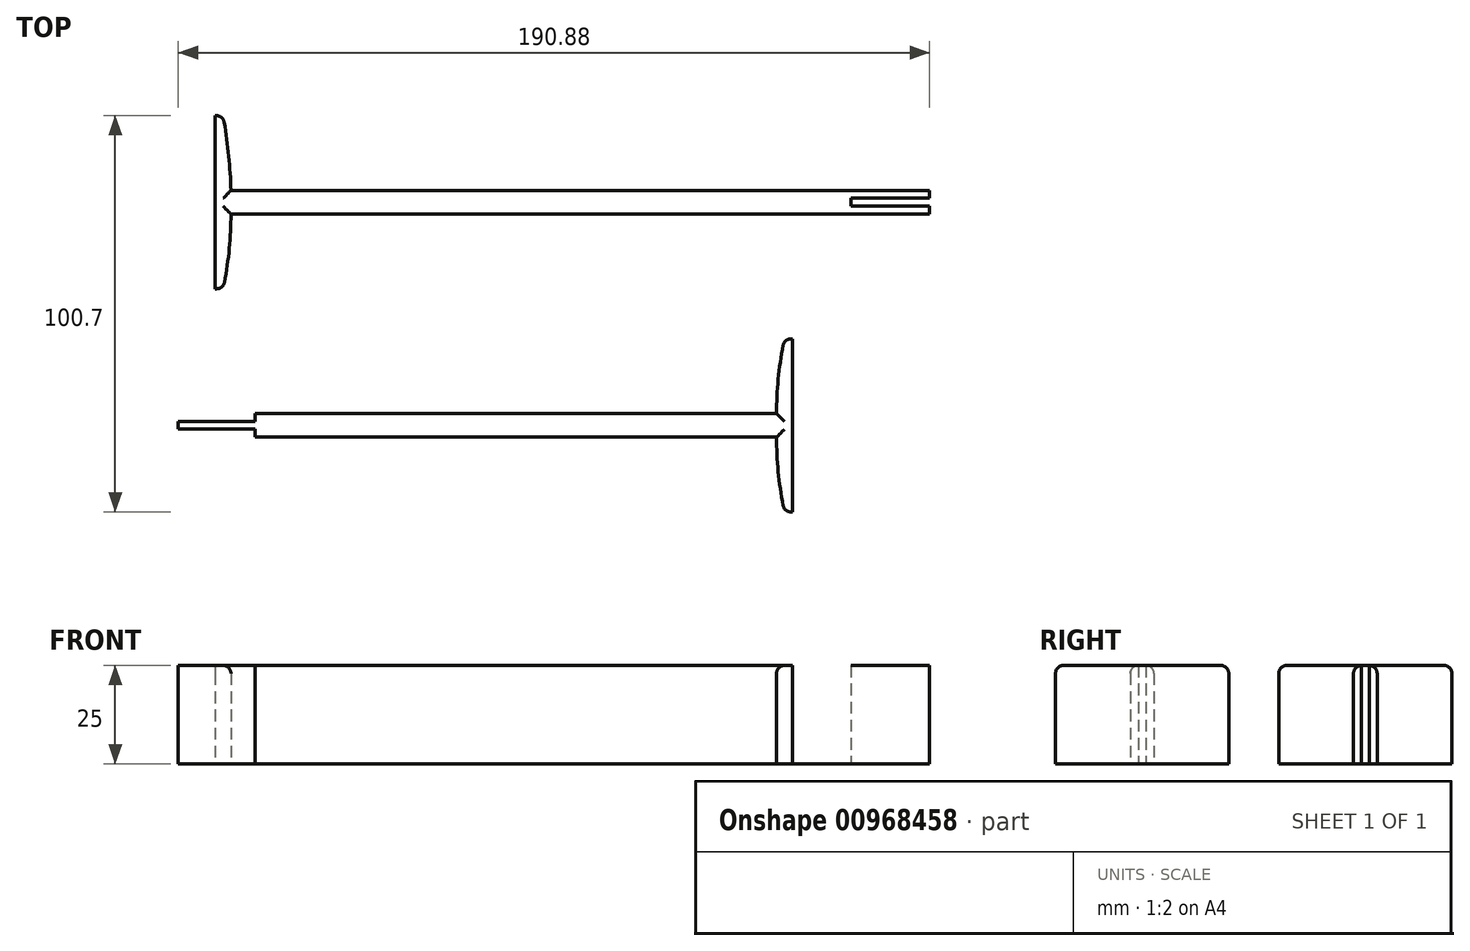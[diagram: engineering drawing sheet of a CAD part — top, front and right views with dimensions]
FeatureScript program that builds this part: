
annotation { "Feature Type Name" : "Feature", "Feature Type Description" : "" }
export const myFeature = defineFeature(function(context is Context, id is Id, definition is map)
    precondition{}
    {
        {
            var Q0;
            Q0=qCreatedBy(makeId("Top.planeOp"),FACE);
            var sketch = newSketch(context, id + "F0", { "sketchPlane" : qUnion([Q0])});
            skLineSegment(sketch, "E0.bottom", {"start": v(-53.26, 18.7) * mm, "end": v(104.24, 18.7) * mm});
            skLineSegment(sketch, "E0.top", {"start": v(-53.26, 12.7) * mm, "end": v(104.24, 12.7) * mm});
            skLineSegment(sketch, "E0.left", {"start": v(-53.26, 18.7) * mm, "end": v(-53.26, 12.7) * mm});
            skLineSegment(sketch, "E0.right", {"start": v(104.24, 18.7) * mm, "end": v(104.24, 12.7) * mm});
            skLineSegment(sketch, "E1.bottom", {"start": v(104.24, 18.7) * mm, "end": v(124.24, 18.7) * mm});
            skLineSegment(sketch, "E1.top", {"start": v(104.24, 16.7) * mm, "end": v(124.24, 16.7) * mm});
            skLineSegment(sketch, "E1.left", {"start": v(104.24, 18.7) * mm, "end": v(104.24, 16.7) * mm});
            skLineSegment(sketch, "E1.right", {"start": v(124.24, 18.7) * mm, "end": v(124.24, 16.7) * mm});
            skLineSegment(sketch, "E2.bottom", {"start": v(104.24, 12.7) * mm, "end": v(124.24, 12.7) * mm});
            skLineSegment(sketch, "E2.top", {"start": v(104.24, 14.7) * mm, "end": v(124.24, 14.7) * mm});
            skLineSegment(sketch, "E2.left", {"start": v(104.24, 12.7) * mm, "end": v(104.24, 14.7) * mm});
            skLineSegment(sketch, "E2.right", {"start": v(124.24, 12.7) * mm, "end": v(124.24, 14.7) * mm});
            skLineSegment(sketch, "E3", {"start": v(-57.26, 37.7) * mm, "end": v(-55.26, 37.7) * mm});
            skLineSegment(sketch, "E4", {"start": v(-57.26, -6.3) * mm, "end": v(-55.26, -6.3) * mm});
            skLineSegment(sketch, "E5", {"start": v(-57.26, -6.3) * mm, "end": v(-57.26, 37.7) * mm});
            skLineSegment(sketch, "E6", {"start": v(-53.26, 18.69) * mm, "end": v(-53.26, 18.7) * mm});
            skLineSegment(sketch, "E7", {"start": v(-53.26, 18.7) * mm, "end": v(-53.26, 18.69) * mm});
            skArc(sketch, "E8", {"start": v(-55.26, -6.3) * mm, "mid": v(-53.76, 3.14) * mm, "end": v(-53.26, 12.7) * mm});
            skArc(sketch, "E9", {"start": v(-53.26, 18.7) * mm, "mid": v(-53.92, 28.23) * mm, "end": v(-55.26, 37.7) * mm});
            skSolve(sketch);
        }
        {
            var Q0;
            Q0=qCreatedBy(makeId("Top.planeOp"),FACE);
            var sketch = newSketch(context, id + "F1", { "sketchPlane" : qUnion([Q0])});
            skLineSegment(sketch, "E10.MirrorCS", {"start": v(-47.14, -38.01) * mm, "end": v(-47.14, -42.01) * mm});
            skLineSegment(sketch, "E11.MirrorCS", {"start": v(-47.14, -38.01) * mm, "end": v(-47.14, -44.01) * mm});
            skLineSegment(sketch, "E12.MirrorCS", {"start": v(85.36, -38.01) * mm, "end": v(85.36, -44.01) * mm});
            skLineSegment(sketch, "E13.MirrorCS", {"start": v(85.36, -44.01) * mm, "end": v(-47.14, -44.01) * mm});
            skLineSegment(sketch, "E14.MirrorCS", {"start": v(85.36, -38.01) * mm, "end": v(-47.14, -38.01) * mm});
            skLineSegment(sketch, "E15.bottom", {"start": v(-47.14, -40.06) * mm, "end": v(-66.64, -40.06) * mm});
            skLineSegment(sketch, "E15.top", {"start": v(-47.14, -41.96) * mm, "end": v(-66.64, -41.96) * mm});
            skLineSegment(sketch, "E15.left", {"start": v(-47.14, -40.06) * mm, "end": v(-47.14, -41.96) * mm});
            skLineSegment(sketch, "E15.right", {"start": v(-66.64, -40.06) * mm, "end": v(-66.64, -41.96) * mm});
            skLineSegment(sketch, "E16", {"start": v(87.36, -19.01) * mm, "end": v(89.36, -19.01) * mm});
            skLineSegment(sketch, "E17", {"start": v(87.36, -63.01) * mm, "end": v(89.36, -63.01) * mm});
            skLineSegment(sketch, "E18", {"start": v(89.36, -63.01) * mm, "end": v(89.36, -19.01) * mm});
            skArc(sketch, "E19", {"start": v(87.36, -19.01) * mm, "mid": v(85.86, -28.46) * mm, "end": v(85.36, -38.01) * mm});
            skArc(sketch, "E20", {"start": v(85.36, -44.01) * mm, "mid": v(85.86, -53.56) * mm, "end": v(87.36, -63.01) * mm});
            skSolve(sketch);
        }
        {
            var Q0;
            Q0=makeQuery(id+"F1.imprint","IMPRINT",FACE,{"disambiguationData":[TD([[makeQuery(id+"F1.imprint","IMPRINT",EDGE,{"derivedFrom":sQuery(id+"F1.wireOp",EDGE,"E12.MirrorCS")}),1.0]])]});
            var Q1;
            Q1=makeQuery(id+"F1.imprint","IMPRINT",FACE,{"disambiguationData":[TD([[makeQuery(id+"F1.imprint","IMPRINT",EDGE,{"derivedFrom":sQuery(id+"F1.wireOp",EDGE,"E12.MirrorCS")}),-1.0]])]});
            var Q2;
            Q2=makeQuery(id+"F1.imprint","IMPRINT",FACE,{"disambiguationData":[TD([[makeQuery(id+"F1.imprint","IMPRINT",EDGE,{"derivedFrom":sQuery(id+"F1.wireOp",EDGE,"E15.bottom")}),1.0]])]});
            var Q3;
            Q3=makeQuery(id+"F0.imprint","IMPRINT",FACE,{"disambiguationData":[TD([[makeQuery(id+"F0.imprint","IMPRINT",EDGE,{"derivedFrom":sQuery(id+"F0.wireOp",EDGE,"E0.left")}),-1.0]])]});
            var Q4;
            Q4=makeQuery(id+"F0.imprint","IMPRINT",FACE,{"disambiguationData":[TD([[makeQuery(id+"F0.imprint","IMPRINT",EDGE,{"derivedFrom":sQuery(id+"F0.wireOp",EDGE,"E0.bottom")}),-1.0]])]});
            var Q5;
            Q5=makeQuery(id+"F0.imprint","IMPRINT",FACE,{"disambiguationData":[TD([[makeQuery(id+"F0.imprint","IMPRINT",EDGE,{"derivedFrom":sQuery(id+"F0.wireOp",EDGE,"E1.bottom")}),-1.0]])]});
            var Q6;
            Q6=makeQuery(id+"F0.imprint","IMPRINT",FACE,{"disambiguationData":[TD([[makeQuery(id+"F0.imprint","IMPRINT",EDGE,{"derivedFrom":sQuery(id+"F0.wireOp",EDGE,"E2.bottom")}),1.0]])]});
            extrude(context, id + "F2", {"entities" : qUnion([Q0, Q1, Q2, Q3, Q4, Q5, Q6]), "depth" : 25 * mm, "offsetDistance" : 25 * mm});
        }
        {
            var Q0;
            Q0=makeQuery(id+"F2.opExtrude","CAP_EDGE",EDGE,{"disambiguationData":[OSD([sQuery(id+"F0.wireOp",EDGE,"E8")])],"isStart":false});
            var Q1;
            Q1=makeQuery(id+"F2.opExtrude","CAP_EDGE",EDGE,{"disambiguationData":[OSD([sQuery(id+"F0.wireOp",EDGE,"E9")])],"isStart":false});
            var Q2;
            Q2=makeQuery(id+"F2.opExtrude","CAP_EDGE",EDGE,{"disambiguationData":[OSD([sQuery(id+"F0.wireOp",EDGE,"E0.bottom"),sQuery(id+"F0.wireOp",EDGE,"E1.bottom")])],"isStart":false});
            var Q3;
            Q3=makeQuery(id+"F2.opExtrude","CAP_EDGE",EDGE,{"disambiguationData":[OSD([sQuery(id+"F0.wireOp",EDGE,"E0.top"),sQuery(id+"F0.wireOp",EDGE,"E2.bottom")])],"isStart":false});
            fillet(context, id + "F3", {"entities" : qUnion([Q0, Q1, Q2, Q3]), "radius" : 2 * mm, "allowEdgeOverflow" : false});
        }
        {
            var Q0;
            Q0=makeQuery(id+"F2.opExtrude","SWEPT_EDGE",EDGE,{"disambiguationData":[OSD([sQuery(id+"F0.wireOp",EDGE,"E4"),sQuery(id+"F0.wireOp",EDGE,"E8")])]});
            var Q1;
            Q1=makeQuery(id+"F2.opExtrude","SWEPT_EDGE",EDGE,{"disambiguationData":[OSD([sQuery(id+"F0.wireOp",EDGE,"E3"),sQuery(id+"F0.wireOp",EDGE,"E9")])]});
            fillet(context, id + "F4", {"entities" : qUnion([Q0, Q1]), "radius" : 2 * mm, "tangentPropagation" : true, "allowEdgeOverflow" : false});
        }
        {
            var Q0;
            Q0=makeQuery(id+"F2.opExtrude","CAP_EDGE",EDGE,{"disambiguationData":[OSD([sQuery(id+"F1.wireOp",EDGE,"E19")])],"isStart":false});
            var Q1;
            Q1=makeQuery(id+"F2.opExtrude","CAP_EDGE",EDGE,{"disambiguationData":[OSD([sQuery(id+"F1.wireOp",EDGE,"E20")])],"isStart":false});
            var Q2;
            Q2=makeQuery(id+"F2.opExtrude","CAP_EDGE",EDGE,{"disambiguationData":[OSD([sQuery(id+"F1.wireOp",EDGE,"E13.MirrorCS")])],"isStart":false});
            var Q3;
            Q3=makeQuery(id+"F2.opExtrude","CAP_EDGE",EDGE,{"disambiguationData":[OSD([sQuery(id+"F1.wireOp",EDGE,"E14.MirrorCS")])],"isStart":false});
            fillet(context, id + "F5", {"entities" : qUnion([Q0, Q1, Q2, Q3]), "radius" : 2 * mm, "allowEdgeOverflow" : false});
        }
        {
            var Q0;
            Q0=makeQuery(id+"F2.opExtrude","SWEPT_EDGE",EDGE,{"disambiguationData":[OSD([sQuery(id+"F1.wireOp",EDGE,"E16"),sQuery(id+"F1.wireOp",EDGE,"E19")])]});
            var Q1;
            Q1=makeQuery(id+"F2.opExtrude","SWEPT_EDGE",EDGE,{"disambiguationData":[OSD([sQuery(id+"F1.wireOp",EDGE,"E17"),sQuery(id+"F1.wireOp",EDGE,"E20")])]});
            fillet(context, id + "F6", {"entities" : qUnion([Q0, Q1]), "radius" : 2 * mm, "tangentPropagation" : true, "allowEdgeOverflow" : false});
        }
    });
